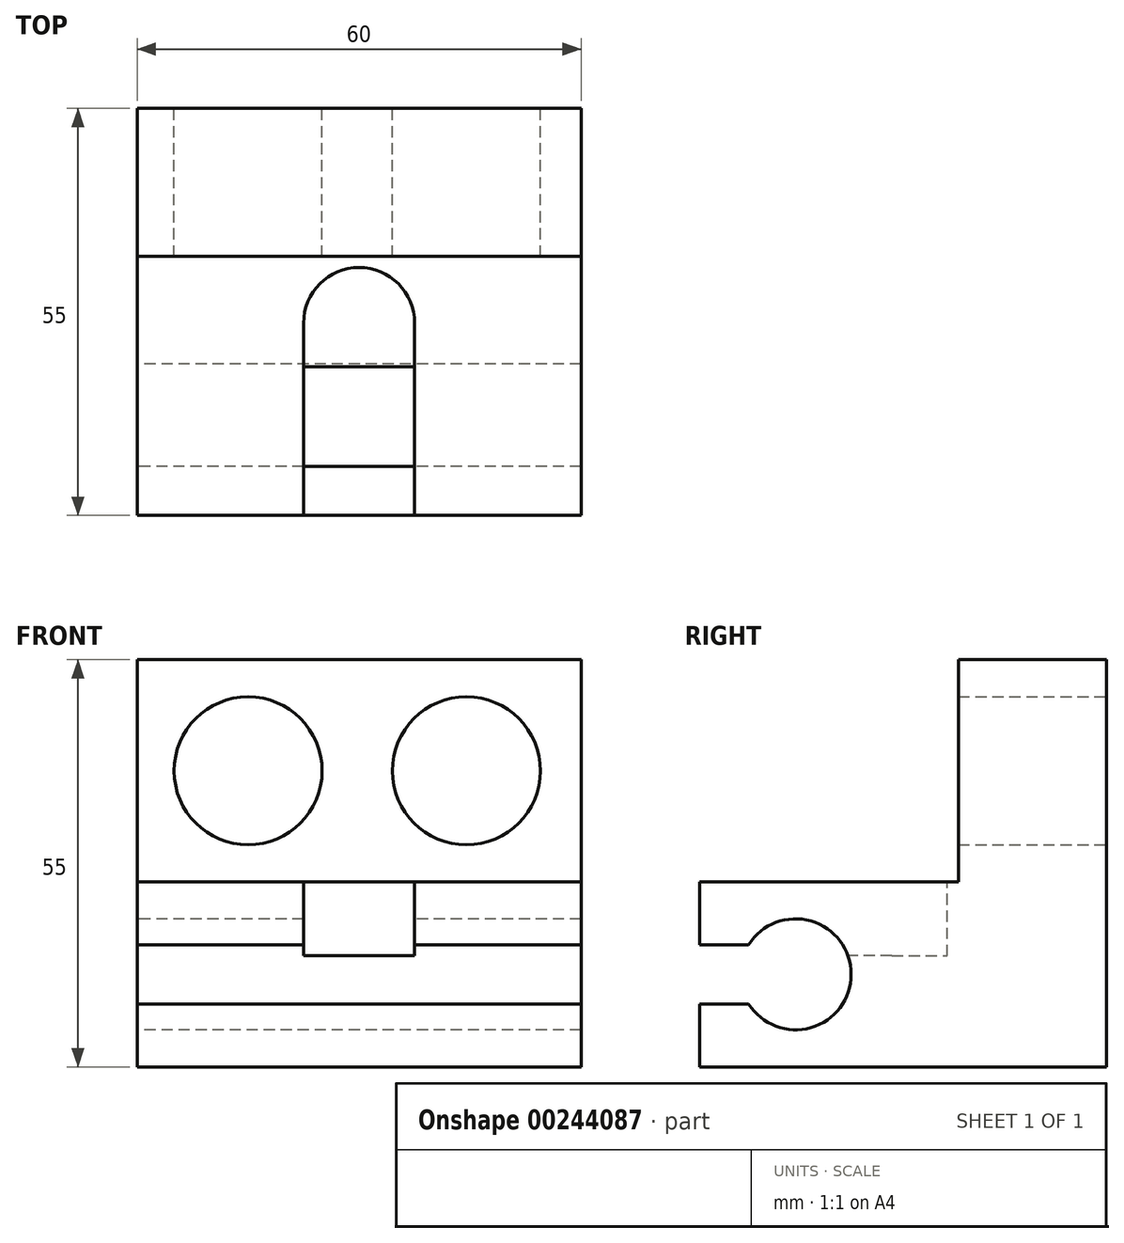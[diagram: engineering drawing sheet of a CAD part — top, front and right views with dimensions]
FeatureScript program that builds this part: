
annotation { "Feature Type Name" : "Feature", "Feature Type Description" : "" }
export const myFeature = defineFeature(function(context is Context, id is Id, definition is map)
    precondition{}
    {
        {
            var Q0;
            Q0=qCreatedBy(makeId("Front.planeOp"),FACE);
            var sketch = newSketch(context, id + "F0", { "sketchPlane" : qUnion([Q0])});
            skLineSegment(sketch, "E0.bottom", {"start": v(-30, -25) * mm, "end": v(30, -25) * mm});
            skLineSegment(sketch, "E0.top", {"start": v(-30, 30) * mm, "end": v(30, 30) * mm});
            skLineSegment(sketch, "E0.left", {"start": v(-30, -25) * mm, "end": v(-30, 30) * mm});
            skLineSegment(sketch, "E0.right", {"start": v(30, -25) * mm, "end": v(30, 30) * mm});
            skCircle(sketch, "E1", {"center": v(-15, 15) * mm, "radius": 10 * mm});
            skCircle(sketch, "E2", {"center": v(14.5, 15) * mm, "radius": 10 * mm});
            skSolve(sketch);
        }
        {
            var Q0;
            Q0 = qSketchRegion(id + "F0", true);
            extrude(context, id + "F1", {"entities" : qUnion([Q0]), "depth" : 20 * mm});
        }
        {
            var Q0;
            Q0=makeQuery(id+"F1.opExtrude","CAP_FACE",FACE,{"disambiguationData":[OSD([sQuery(id+"F0.wireOp",EDGE,"E0.bottom"),sQuery(id+"F0.wireOp",EDGE,"E0.top"),sQuery(id+"F0.wireOp",EDGE,"E0.left"),sQuery(id+"F0.wireOp",EDGE,"E0.right"),sQuery(id+"F0.wireOp",EDGE,"E1"),sQuery(id+"F0.wireOp",EDGE,"E2")])],"isStart":false});
            var sketch = newSketch(context, id + "F2", { "sketchPlane" : qUnion([Q0])});
            skLineSegment(sketch, "E3.bottom", {"start": v(-30, -25) * mm, "end": v(30, -25) * mm});
            skLineSegment(sketch, "E3.top", {"start": v(-30, 0) * mm, "end": v(30, 0) * mm});
            skLineSegment(sketch, "E3.left", {"start": v(-30, -25) * mm, "end": v(-30, 0) * mm});
            skLineSegment(sketch, "E3.right", {"start": v(30, -25) * mm, "end": v(30, 0) * mm});
            skSolve(sketch);
        }
        {
            var Q0;
            Q0 = qSketchRegion(id + "F2", true);
            extrude(context, id + "F3", {"entities" : qUnion([Q0]), "operationType" : NewBodyOperationType.ADD, "depth" : 35 * mm});
        }
        {
            var Q0;
            Q0=makeQuery(id+"F3.boolean.opBoolean","MERGE",FACE,{"derivedFrom":[makeQuery(id+"F1.opExtrude","SWEPT_FACE",FACE,{"disambiguationData":[OSD([sQuery(id+"F0.wireOp",EDGE,"E0.left")])]}),makeQuery(id+"F3.opExtrude","SWEPT_FACE",FACE,{"disambiguationData":[OSD([sQuery(id+"F2.wireOp",EDGE,"E3.left")])]})]});
            var sketch = newSketch(context, id + "F4", { "sketchPlane" : qUnion([Q0])});
            skCircle(sketch, "E4", {"center": v(42, -12.5) * mm, "radius": 7.5 * mm});
            skSolve(sketch);
        }
        {
            var Q0;
            Q0 = qSketchRegion(id + "F4", true);
            extrude(context, id + "F5", {"entities" : qUnion([Q0]), "operationType" : NewBodyOperationType.REMOVE, "endBound" : BoundingType.THROUGH_ALL, "oppositeDirection" : true, "depth" : 25 * mm});
        }
        {
            var Q0;
            Q0=makeQuery(id+"F3.opExtrude","SWEPT_FACE",FACE,{"disambiguationData":[OSD([sQuery(id+"F2.wireOp",EDGE,"E3.top")])]});
            var sketch = newSketch(context, id + "F6", { "sketchPlane" : qUnion([Q0])});
            skLineSegment(sketch, "E5.top", {"start": v(7.5, -55) * mm, "end": v(-7.5, -55) * mm});
            skLineSegment(sketch, "E5.left", {"start": v(7.5, -29) * mm, "end": v(7.5, -55) * mm});
            skLineSegment(sketch, "E5.right", {"start": v(-7.5, -29) * mm, "end": v(-7.5, -55) * mm});
            skArc(sketch, "E6", {"start": v(7.5, -29) * mm, "mid": v(0, -21.5) * mm, "end": v(-7.5, -29) * mm});
            skSolve(sketch);
        }
        {
            var Q0;
            Q0 = qSketchRegion(id + "F6", true);
            extrude(context, id + "F7", {"entities" : qUnion([Q0]), "operationType" : NewBodyOperationType.REMOVE, "oppositeDirection" : true, "depth" : 10 * mm});
        }
        {
            var Q0;
            {var subQ0=sQuery(id+"F2.wireOp",EDGE,"E3.top");var subQ1=sQuery(id+"F2.wireOp",EDGE,"E3.bottom");var subQ2=sQuery(id+"F2.wireOp",EDGE,"E3.left");Q0=makeQuery(id+"F7.boolean.opBoolean","SPLIT",FACE,{"disambiguationData":[TD([makeQuery(id+"F1.opExtrude","SWEPT_FACE",FACE,{"disambiguationData":[OSD([sQuery(id+"F0.wireOp",EDGE,"E0.left")])]})])],"derivedFrom":makeQuery(id+"F3.opExtrude","CAP_FACE",FACE,{"disambiguationData":[OSD([subQ1,subQ0,subQ2,sQuery(id+"F2.wireOp",EDGE,"E3.right")])],"isStart":false})});}
            var sketch = newSketch(context, id + "F8", { "sketchPlane" : qUnion([Q0])});
            skLineSegment(sketch, "E7.bottom", {"start": v(-30, -8.5) * mm, "end": v(30, -8.5) * mm});
            skLineSegment(sketch, "E7.top", {"start": v(-30, -16.5) * mm, "end": v(30, -16.5) * mm});
            skLineSegment(sketch, "E7.left", {"start": v(-30, -8.5) * mm, "end": v(-30, -16.5) * mm});
            skLineSegment(sketch, "E7.right", {"start": v(30, -8.5) * mm, "end": v(30, -16.5) * mm});
            skSolve(sketch);
        }
        {
            var Q0;
            Q0 = qSketchRegion(id + "F8", true);
            extrude(context, id + "F9", {"entities" : qUnion([Q0]), "operationType" : NewBodyOperationType.REMOVE, "oppositeDirection" : true, "depth" : 8 * mm});
        }
        {
            var Q0;
            Q0=makeQuery(id+"F1.opExtrude","SWEPT_BODY",BODY,{"disambiguationData":[OSD([sQuery(id+"F0.wireOp",EDGE,"E0.bottom"),sQuery(id+"F0.wireOp",EDGE,"E0.top"),sQuery(id+"F0.wireOp",EDGE,"E0.left"),sQuery(id+"F0.wireOp",EDGE,"E0.right"),sQuery(id+"F0.wireOp",EDGE,"E1"),sQuery(id+"F0.wireOp",EDGE,"E2")])]});
            var Q1;
            Q1=makeQuery(id+"F1.opExtrude","CAP_EDGE",EDGE,{"disambiguationData":[OSD([sQuery(id+"F0.wireOp",EDGE,"E0.left")])],"isStart":true});
            transform(context, id + "F10", {"entities" : qUnion([Q0]), "transformType" : TransformType.TRANSLATION_3D, "dx" : -30 * mm, "dy" : 0 * mm, "dz" : -30 * mm, "makeCopy" : false});
        }
    });
